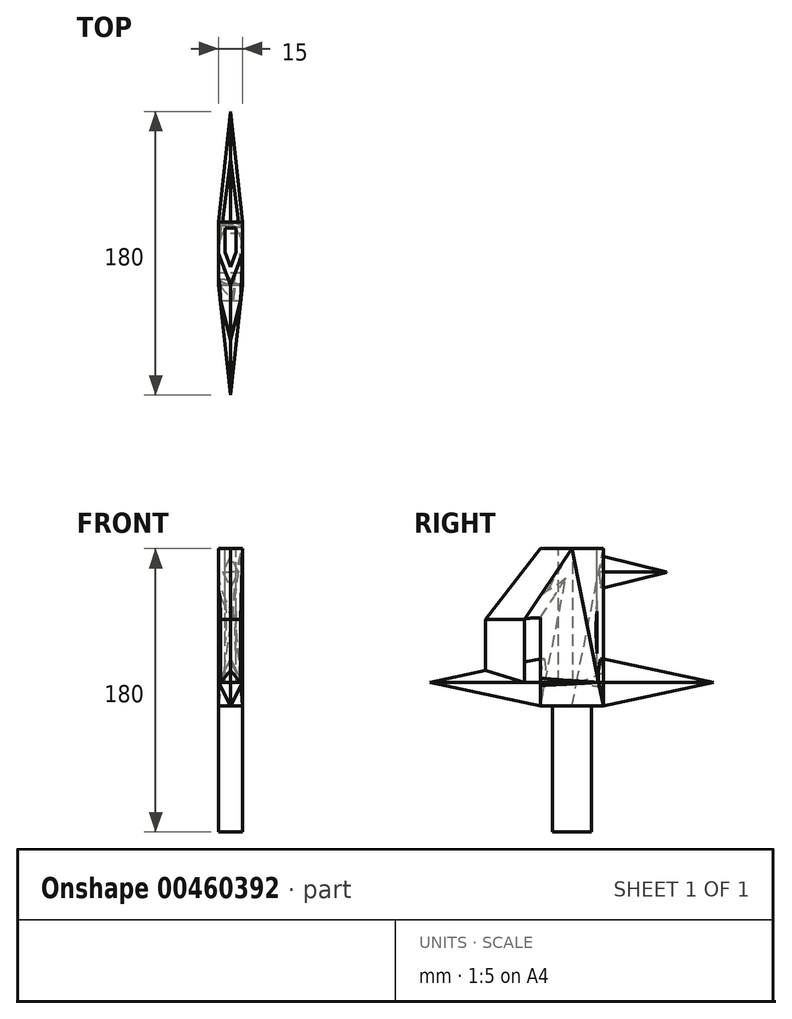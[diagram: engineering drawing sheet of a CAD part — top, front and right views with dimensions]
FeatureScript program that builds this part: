
annotation { "Feature Type Name" : "Feature", "Feature Type Description" : "" }
export const myFeature = defineFeature(function(context is Context, id is Id, definition is map)
    precondition{}
    {
        {
            var Q0;
            Q0=qCreatedBy(makeId("Top.planeOp"),FACE);
            var sketch = newSketch(context, id + "F0", { "sketchPlane" : qUnion([Q0])});
            skLineSegment(sketch, "E0.bottom", {"start": v(7.5, 20) * mm, "end": v(-7.5, 20) * mm});
            skLineSegment(sketch, "E0.top", {"start": v(7.5, -20) * mm, "end": v(-7.5, -20) * mm});
            skLineSegment(sketch, "E0.left", {"start": v(7.5, 20) * mm, "end": v(7.5, -20) * mm});
            skLineSegment(sketch, "E0.right", {"start": v(-7.5, 20) * mm, "end": v(-7.5, -20) * mm});
            skPoint(sketch, "E0.middle", {"position": v(0, 0) * mm});
            skSolve(sketch);
        }
        {
            var Q0;
            Q0=qCreatedBy(makeId("Top.planeOp"),FACE);
            cPlane(context, id + "F1", {"entities" : qUnion([Q0]), "cplaneType" : CPlaneType.OFFSET, "offset" : 100 * mm, "width" : 150 * mm, "height" : 150 * mm});
        }
        {
            var Q0;
            Q0=qCreatedBy(id+"F1.planeOp",FACE);
            var sketch = newSketch(context, id + "F2", { "sketchPlane" : qUnion([Q0])});
            skLineSegment(sketch, "E1", {"start": v(-7.5, 20) * mm, "end": v(7.5, 20) * mm});
            skLineSegment(sketch, "E2", {"start": v(7.5, 20) * mm, "end": v(7.5, 0) * mm});
            skLineSegment(sketch, "E3", {"start": v(7.5, 0) * mm, "end": v(0, -20) * mm});
            skLineSegment(sketch, "E4", {"start": v(0, -20) * mm, "end": v(-7.5, 0) * mm});
            skLineSegment(sketch, "E5", {"start": v(-7.5, 0) * mm, "end": v(-7.5, 20) * mm});
            skSolve(sketch);
        }
        {
            var Q0;
            Q0=makeQuery(id+"F0.imprint","IMPRINT",FACE,{"disambiguationData":[TD([[makeQuery(id+"F0.imprint","IMPRINT",EDGE,{"derivedFrom":sQuery(id+"F0.wireOp",EDGE,"E0.bottom")}),1.0]])]});
            var Q1;
            Q1=makeQuery(id+"F2.imprint","IMPRINT",FACE,{"disambiguationData":[TD([[makeQuery(id+"F2.imprint","IMPRINT",EDGE,{"derivedFrom":sQuery(id+"F2.wireOp",EDGE,"E1")}),-1.0]])]});
            var Q2;
            Q2=sQuery(id+"F2.wireOp",VERTEX,"E5.start");
            var Q3;
            Q3=sQuery(id+"F0.wireOp",VERTEX,"E0.right.end");
            loft(context, id + "F3", {"sheetProfilesArray" : [{ "sheetProfileEntities" : qUnion([Q0]) }, { "sheetProfileEntities" : qUnion([Q1]) }], "matchConnections" : true, "connections" : [{ "connectionEntities" : qUnion([Q2, Q3]), "connectionEdgeQueries" : qUnion([]), "connectionEdgeParameters" : [] }]});
        }
        {
            var Q0;
            Q0=makeQuery(id+"F3.opLoft","CAP_FACE",FACE,{"disambiguationData":[OSD([makeQuery(id+"F0.imprint","IMPRINT",FACE,{"disambiguationData":[TD([[makeQuery(id+"F0.imprint","IMPRINT",EDGE,{"derivedFrom":sQuery(id+"F0.wireOp",EDGE,"E0.bottom")}),1.0]])]})])],"isStart":true});
            var sketch = newSketch(context, id + "F4", { "sketchPlane" : qUnion([Q0])});
            skLineSegment(sketch, "E6.bottom", {"start": v(7.5, -12.5) * mm, "end": v(-7.5, -12.5) * mm});
            skLineSegment(sketch, "E6.top", {"start": v(7.5, 12.5) * mm, "end": v(-7.5, 12.5) * mm});
            skLineSegment(sketch, "E6.left", {"start": v(7.5, -12.5) * mm, "end": v(7.5, 12.5) * mm});
            skLineSegment(sketch, "E6.right", {"start": v(-7.5, -12.5) * mm, "end": v(-7.5, 12.5) * mm});
            skPoint(sketch, "E6.middle", {"position": v(0, 0) * mm});
            skSolve(sketch);
        }
        {
            var Q0;
            Q0 = qSketchRegion(id + "F4", true);
            extrude(context, id + "F5", {"entities" : qUnion([Q0]), "operationType" : NewBodyOperationType.ADD, "depth" : 80 * mm});
        }
        {
            var Q0;
            Q0=qCreatedBy(makeId("Front.planeOp"),FACE);
            var sketch = newSketch(context, id + "F6", { "sketchPlane" : qUnion([Q0])});
            skLineSegment(sketch, "E7", {"start": v(0, 0) * mm, "end": v(7.5, 15) * mm});
            skLineSegment(sketch, "E8", {"start": v(7.5, 15) * mm, "end": v(0, 30) * mm});
            skLineSegment(sketch, "E9", {"start": v(0, 30) * mm, "end": v(-7.5, 15) * mm});
            skLineSegment(sketch, "E10", {"start": v(-7.5, 15) * mm, "end": v(0, 0) * mm});
            skLineSegment(sketch, "E11", {"start": v(0, 30) * mm, "end": v(0, 0) * mm, "construction": true});
            skPoint(sketch, "E12", {"position": v(0, 15) * mm});
            skSolve(sketch);
        }
        {
            var Q0;
            Q0 = qSketchRegion(id + "F6", true);
            extrude(context, id + "F7", {"entities" : qUnion([Q0]), "operationType" : NewBodyOperationType.ADD, "endBound" : BoundingType.SYMMETRIC, "oppositeDirection" : true, "depth" : 180 * mm, "offsetDistance" : 25 * mm});
        }
        {
            var Q0;
            Q0=makeQuery(id+"F7.opExtrude","CAP_FACE",FACE,{"disambiguationData":[OSD([sQuery(id+"F6.wireOp",EDGE,"E7"),sQuery(id+"F6.wireOp",EDGE,"E8"),sQuery(id+"F6.wireOp",EDGE,"E9"),sQuery(id+"F6.wireOp",EDGE,"E10")])],"isStart":false});
            chamfer(context, id + "F8", {"entities" : qUnion([Q0]), "chamferType" : ChamferType.TWO_OFFSETS, "width1" : 70 * mm, "oppositeDirection" : false, "width2" : 6.7 * mm, "tangentPropagation" : true});
        }
        {
            var Q0;
            Q0=makeQuery(id+"F7.opExtrude","CAP_FACE",FACE,{"disambiguationData":[OSD([sQuery(id+"F6.wireOp",EDGE,"E7"),sQuery(id+"F6.wireOp",EDGE,"E8"),sQuery(id+"F6.wireOp",EDGE,"E9"),sQuery(id+"F6.wireOp",EDGE,"E10")])],"isStart":true});
            chamfer(context, id + "F9", {"entities" : qUnion([Q0]), "chamferType" : ChamferType.TWO_OFFSETS, "width1" : 6.7 * mm, "oppositeDirection" : false, "width2" : 70 * mm, "tangentPropagation" : true});
        }
        {
            var Q0;
            Q0=qCreatedBy(makeId("Front.planeOp"),FACE);
            var sketch = newSketch(context, id + "F10", { "sketchPlane" : qUnion([Q0])});
            skLineSegment(sketch, "E13", {"start": v(0, 75) * mm, "end": v(-5, 85) * mm});
            skLineSegment(sketch, "E14", {"start": v(-5, 85) * mm, "end": v(0, 95) * mm});
            skLineSegment(sketch, "E15", {"start": v(0, 95) * mm, "end": v(5, 85) * mm});
            skLineSegment(sketch, "E16", {"start": v(5, 85) * mm, "end": v(0, 75) * mm});
            skLineSegment(sketch, "E17", {"start": v(0, 95) * mm, "end": v(0, 75) * mm, "construction": true});
            skPoint(sketch, "E18", {"position": v(0, 85) * mm});
            skSolve(sketch);
        }
        {
            var Q0;
            Q0 = qSketchRegion(id + "F10", true);
            extrude(context, id + "F11", {"entities" : qUnion([Q0]), "operationType" : NewBodyOperationType.ADD, "oppositeDirection" : true, "depth" : 60 * mm, "offsetDistance" : 25 * mm});
        }
        {
            var Q0;
            Q0=makeQuery(id+"F11.opExtrude","CAP_FACE",FACE,{"disambiguationData":[OSD([sQuery(id+"F10.wireOp",EDGE,"E13"),sQuery(id+"F10.wireOp",EDGE,"E14"),sQuery(id+"F10.wireOp",EDGE,"E15"),sQuery(id+"F10.wireOp",EDGE,"E16")])],"isStart":false});
            chamfer(context, id + "F12", {"entities" : qUnion([Q0]), "chamferType" : ChamferType.TWO_OFFSETS, "width1" : 4.4 * mm, "oppositeDirection" : false, "width2" : 40 * mm, "tangentPropagation" : true});
        }
        {
            var Q0;
            {var subQ0=sQuery(id+"F6.wireOp",EDGE,"E9");var subQ1=sQuery(id+"F6.wireOp",EDGE,"E8");Q0=makeQuery(id+"F9.opChamfer","BLEND_VERTEX",VERTEX,{"blendedFrom":[makeQuery(id+"F7.opExtrude","CAP_EDGE",EDGE,{"disambiguationData":[OSD([subQ1])],"isStart":true}),makeQuery(id+"F7.opExtrude","CAP_EDGE",EDGE,{"disambiguationData":[OSD([subQ0])],"isStart":true}),makeQuery(id+"F7.opExtrude","CAP_FACE",FACE,{"disambiguationData":[OSD([sQuery(id+"F6.wireOp",EDGE,"E7"),subQ1,subQ0,sQuery(id+"F6.wireOp",EDGE,"E10")])],"isStart":true})],"blendedInto":[makeQuery(id+"F7.opExtrude","CAP_FACE",FACE,{"disambiguationData":[OSD([sQuery(id+"F6.wireOp",EDGE,"E7"),subQ1,subQ0,sQuery(id+"F6.wireOp",EDGE,"E10")])],"isStart":true})]});}
            var Q1;
            {var subQ11=sQuery(id+"F6.wireOp",EDGE,"E7");var subQ12=sQuery(id+"F6.wireOp",EDGE,"E10");var subQ13=sQuery(id+"F6.wireOp",EDGE,"E9");var subQ14=sQuery(id+"F6.wireOp",EDGE,"E8");var subQ15=makeQuery(id+"F7.opExtrude","CAP_FACE",FACE,{"disambiguationData":[OSD([subQ11,subQ14,subQ13,subQ12])],"isStart":true});var subQ16=makeQuery(id+"F7.opExtrude","SWEPT_FACE",FACE,{"disambiguationData":[OSD([subQ13])]});var subQ17=makeQuery(id+"F7.opExtrude","SWEPT_FACE",FACE,{"disambiguationData":[OSD([subQ12])]});Q1=makeQuery(id+"F9.opChamfer","BLEND_VERTEX",VERTEX,{"blendedFrom":[makeQuery(id+"F7.opExtrude","CAP_EDGE",EDGE,{"disambiguationData":[OSD([subQ13])],"isStart":true}),makeQuery(id+"F7.opExtrude","CAP_EDGE",EDGE,{"disambiguationData":[OSD([subQ12])],"isStart":true}),makeQuery(id+"F7.boolean.opBoolean","SPLIT",FACE,{"disambiguationData":[TD([subQ15])],"derivedFrom":subQ16}),makeQuery(id+"F7.boolean.opBoolean","SPLIT",FACE,{"disambiguationData":[TD([subQ15])],"derivedFrom":subQ17})],"blendedInto":[makeQuery(id+"F7.boolean.opBoolean","SPLIT",FACE,{"disambiguationData":[TD([subQ15])],"derivedFrom":subQ16}),makeQuery(id+"F7.boolean.opBoolean","SPLIT",FACE,{"disambiguationData":[TD([subQ15])],"derivedFrom":subQ17})]});}
            var Q2;
            {var subQ12=sQuery(id+"F6.wireOp",EDGE,"E7");var subQ13=makeQuery(id+"F7.opExtrude","SWEPT_FACE",FACE,{"disambiguationData":[OSD([subQ12])]});var subQ14=sQuery(id+"F6.wireOp",EDGE,"E10");var subQ15=sQuery(id+"F6.wireOp",EDGE,"E9");var subQ16=sQuery(id+"F6.wireOp",EDGE,"E8");var subQ17=makeQuery(id+"F7.opExtrude","CAP_FACE",FACE,{"disambiguationData":[OSD([subQ12,subQ16,subQ15,subQ14])],"isStart":true});var subQ18=makeQuery(id+"F7.opExtrude","SWEPT_FACE",FACE,{"disambiguationData":[OSD([subQ16])]});Q2=makeQuery(id+"F9.opChamfer","BLEND_VERTEX",VERTEX,{"blendedFrom":[makeQuery(id+"F7.opExtrude","CAP_EDGE",EDGE,{"disambiguationData":[OSD([subQ12])],"isStart":true}),makeQuery(id+"F7.opExtrude","CAP_EDGE",EDGE,{"disambiguationData":[OSD([subQ16])],"isStart":true}),makeQuery(id+"F7.boolean.opBoolean","SPLIT",FACE,{"disambiguationData":[TD([subQ17])],"derivedFrom":subQ13}),makeQuery(id+"F7.boolean.opBoolean","SPLIT",FACE,{"disambiguationData":[TD([subQ17])],"derivedFrom":subQ18})],"blendedInto":[makeQuery(id+"F7.boolean.opBoolean","SPLIT",FACE,{"disambiguationData":[TD([subQ17])],"derivedFrom":subQ13}),makeQuery(id+"F7.boolean.opBoolean","SPLIT",FACE,{"disambiguationData":[TD([subQ17])],"derivedFrom":subQ18})]});}
            cPlane(context, id + "F13", {"entities" : qUnion([Q0, Q1, Q2]), "cplaneType" : CPlaneType.THREE_POINT, "offset" : 25 * mm, "width" : 150 * mm, "height" : 150 * mm});
        }
        {
            var Q0;
            Q0=qCreatedBy(id+"F13.planeOp",FACE);
            var sketch = newSketch(context, id + "F14", { "sketchPlane" : qUnion([Q0])});
            skLineSegment(sketch, "E19", {"start": v(-6.43, -30.03) * mm, "end": v(6.43, -30.03) * mm});
            skLineSegment(sketch, "E20", {"start": v(6.43, -30.03) * mm, "end": v(0, -55.03) * mm});
            skLineSegment(sketch, "E21", {"start": v(0, -55.03) * mm, "end": v(-6.43, -30.03) * mm});
            skSolve(sketch);
        }
        {
            var Q0;
            Q0 = qSketchRegion(id + "F14", true);
            extrude(context, id + "F15", {"entities" : qUnion([Q0]), "operationType" : NewBodyOperationType.ADD, "depth" : 40 * mm});
        }
        {
            var Q0;
            Q0=makeQuery(id+"F3.opLoft","CAP_FACE",FACE,{"disambiguationData":[OSD([makeQuery(id+"F2.imprint","IMPRINT",FACE,{"disambiguationData":[TD([[makeQuery(id+"F2.imprint","IMPRINT",EDGE,{"derivedFrom":sQuery(id+"F2.wireOp",EDGE,"E1")}),-1.0]])]})])],"isStart":true});
            var sketch = newSketch(context, id + "F16", { "sketchPlane" : qUnion([Q0])});
            skLineSegment(sketch, "E22", {"start": v(-7.5, 0) * mm, "end": v(7.5, 0) * mm});
            skLineSegment(sketch, "E23", {"start": v(7.5, 0) * mm, "end": v(0, -20) * mm});
            skLineSegment(sketch, "E24", {"start": v(0, -20) * mm, "end": v(-7.5, 0) * mm});
            skSolve(sketch);
        }
        {
            var Q1;
            Q1=makeQuery(id+"F15.opExtrude","CAP_FACE",FACE,{"disambiguationData":[OSD([sQuery(id+"F14.wireOp",EDGE,"E19"),sQuery(id+"F14.wireOp",EDGE,"E20"),sQuery(id+"F14.wireOp",EDGE,"E21")])],"isStart":false});
            var Q2;
            Q2 = qSketchRegion(id + "F16", true);
            loft(context, id + "F17", {"operationType" : NewBodyOperationType.ADD, "sheetProfilesArray" : [{ "sheetProfileEntities" : qUnion([Q1]) }, { "sheetProfileEntities" : qUnion([Q2]) }]});
        }
        {
            var Q0;
            {var subQ0=sQuery(id+"F2.wireOp",EDGE,"E5");var subQ1=sQuery(id+"F2.wireOp",EDGE,"E4");var subQ2=sQuery(id+"F2.wireOp",EDGE,"E3");var subQ3=sQuery(id+"F2.wireOp",EDGE,"E2");var subQ4=sQuery(id+"F2.wireOp",EDGE,"E1");var subQ5=sQuery(id+"F0.wireOp",EDGE,"E0.top");var subQ6=sQuery(id+"F0.wireOp",EDGE,"E0.left");var subQ7=makeQuery(id+"F3.opLoft","SWEPT_FACE",FACE,{"disambiguationData":[OSD([subQ5,subQ6,subQ3,subQ2,subQ1,subQ0])]});Q0=makeQuery(id+"F17.boolean.opBoolean","INTERSECT",EDGE,{"derivedFrom":[makeQuery(id+"F7.boolean.opBoolean","SPLIT",FACE,{"disambiguationData":[TD([makeQuery(id+"F7.opExtrude","SWEPT_FACE",FACE,{"disambiguationData":[OSD([sQuery(id+"F6.wireOp",EDGE,"E9")])]})])],"derivedFrom":subQ7}),makeQuery(id+"F17.opLoft","SWEPT_FACE",FACE,{"disambiguationData":[OSD([subQ4,subQ3,subQ2,subQ1,subQ0,sQuery(id+"F14.wireOp",EDGE,"E19"),sQuery(id+"F14.wireOp",EDGE,"E20"),sQuery(id+"F14.wireOp",EDGE,"E21"),sQuery(id+"F16.wireOp",EDGE,"E22"),sQuery(id+"F16.wireOp",EDGE,"E23"),sQuery(id+"F16.wireOp",EDGE,"E24")])]})]});}
            var Q1;
            {var subQ0=sQuery(id+"F2.wireOp",EDGE,"E5");var subQ1=sQuery(id+"F2.wireOp",EDGE,"E4");var subQ2=sQuery(id+"F2.wireOp",EDGE,"E3");var subQ3=sQuery(id+"F2.wireOp",EDGE,"E2");var subQ4=sQuery(id+"F2.wireOp",EDGE,"E1");var subQ5=sQuery(id+"F0.wireOp",EDGE,"E0.right");var subQ6=sQuery(id+"F0.wireOp",EDGE,"E0.top");var subQ7=makeQuery(id+"F3.opLoft","SWEPT_FACE",FACE,{"disambiguationData":[OSD([subQ6,subQ5,subQ2,subQ1,subQ0])]});Q1=makeQuery(id+"F17.boolean.opBoolean","INTERSECT",EDGE,{"derivedFrom":[makeQuery(id+"F7.boolean.opBoolean","SPLIT",FACE,{"disambiguationData":[TD([makeQuery(id+"F7.opExtrude","SWEPT_FACE",FACE,{"disambiguationData":[OSD([sQuery(id+"F6.wireOp",EDGE,"E8")])]})])],"derivedFrom":subQ7}),makeQuery(id+"F17.opLoft","SWEPT_FACE",FACE,{"disambiguationData":[OSD([subQ4,subQ3,subQ2,subQ1,subQ0,sQuery(id+"F14.wireOp",EDGE,"E19"),sQuery(id+"F14.wireOp",EDGE,"E20"),sQuery(id+"F14.wireOp",EDGE,"E21"),sQuery(id+"F16.wireOp",EDGE,"E22"),sQuery(id+"F16.wireOp",EDGE,"E23"),sQuery(id+"F16.wireOp",EDGE,"E24")])]})]});}
            chamfer(context, id + "F18", {"entities" : qUnion([Q0, Q1]), "width" : 5 * mm, "tangentPropagation" : true});
        }
        {
            var Q0;
            Q0=makeQuery(id+"F3.opLoft","CAP_FACE",FACE,{"disambiguationData":[OSD([makeQuery(id+"F2.imprint","IMPRINT",FACE,{"disambiguationData":[TD([[makeQuery(id+"F2.imprint","IMPRINT",EDGE,{"derivedFrom":sQuery(id+"F2.wireOp",EDGE,"E1")}),-1.0]])]})])],"isStart":true});
            var sketch = newSketch(context, id + "F19", { "sketchPlane" : qUnion([Q0])});
            skLineSegment(sketch, "E25.0", {"start": v(-3.5, 0.73) * mm, "end": v(0, -8.6) * mm});
            skLineSegment(sketch, "E25.1", {"start": v(-3.5, 16) * mm, "end": v(-3.5, 0.73) * mm});
            skLineSegment(sketch, "E25.2", {"start": v(0, -8.6) * mm, "end": v(3.5, 0.73) * mm});
            skLineSegment(sketch, "E25.3", {"start": v(3.5, 0.73) * mm, "end": v(3.5, 16) * mm});
            skLineSegment(sketch, "E25.4", {"start": v(3.5, 16) * mm, "end": v(-3.5, 16) * mm});
            skSolve(sketch);
        }
        {
            var Q0;
            Q0=makeQuery(id+"F19.imprint","IMPRINT",FACE,{"disambiguationData":[TD([[makeQuery(id+"F19.imprint","IMPRINT",EDGE,{"derivedFrom":sQuery(id+"F19.wireOp",EDGE,"E25.0")}),1.0]])]});
            extrude(context, id + "F20", {"entities" : qUnion([Q0]), "operationType" : NewBodyOperationType.REMOVE, "oppositeDirection" : true, "depth" : 85 * mm, "offsetDistance" : 25 * mm});
        }
    });
